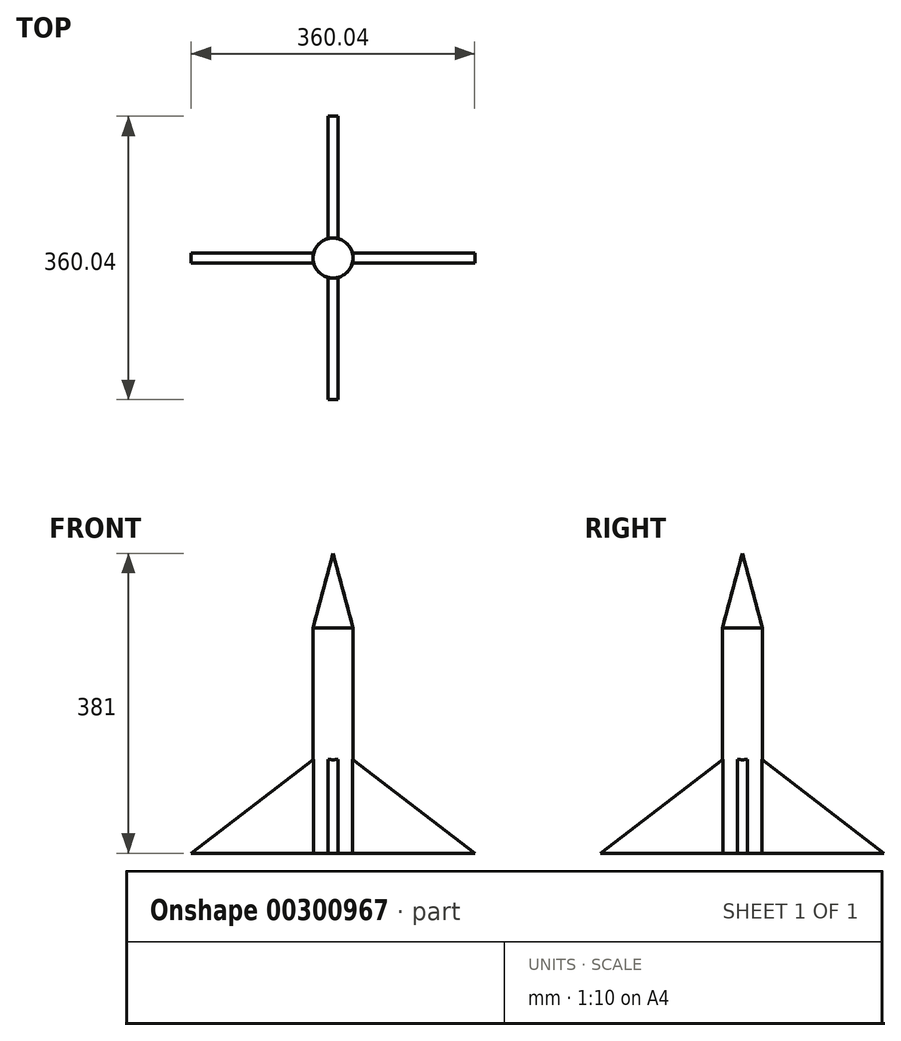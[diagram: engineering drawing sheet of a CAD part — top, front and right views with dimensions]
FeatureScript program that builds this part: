
annotation { "Feature Type Name" : "Feature", "Feature Type Description" : "" }
export const myFeature = defineFeature(function(context is Context, id is Id, definition is map)
    precondition{}
    {
        {
            var Q0;
            Q0=qCreatedBy(makeId("Top.planeOp"),FACE);
            var sketch = newSketch(context, id + "F0", { "sketchPlane" : qUnion([Q0])});
            skCircle(sketch, "E0", {"center": v(0, 0) * mm, "radius": 25.4 * mm});
            skSolve(sketch);
        }
        {
            var Q0;
            Q0 = qSketchRegion(id + "F0", true);
            extrude(context, id + "F1", {"entities" : qUnion([Q0]), "depth" : 381 * mm});
        }
        {
            var Q0;
            Q0=makeQuery(id+"F1.opExtrude","CAP_EDGE",EDGE,{"disambiguationData":[OSD([sQuery(id+"F0.wireOp",EDGE,"E0")])],"isStart":false});
            chamfer(context, id + "F2", {"entities" : qUnion([Q0]), "chamferType" : ChamferType.OFFSET_ANGLE, "width" : 25.4 * mm, "oppositeDirection" : false, "angle" : 75 * degree, "tangentPropagation" : true});
        }
        {
            var Q0;
            Q0=qCreatedBy(makeId("Front.planeOp"),FACE);
            var sketch = newSketch(context, id + "F3", { "sketchPlane" : qUnion([Q0])});
            skLineSegment(sketch, "E1", {"start": v(0, 138.23) * mm, "end": v(0, 0) * mm});
            skLineSegment(sketch, "E2", {"start": v(180.02, 0) * mm, "end": v(0, 0) * mm});
            skLineSegment(sketch, "E3", {"start": v(-129.4, 68.74) * mm, "end": v(-118.85, 63.14) * mm});
            skLineSegment(sketch, "E4", {"start": v(0, 138.23) * mm, "end": v(180.02, 0) * mm});
            skSolve(sketch);
        }
        {
            var Q0;
            Q0 = qSketchRegion(id + "F3", true);
            extrude(context, id + "F4", {"entities" : qUnion([Q0]), "operationType" : NewBodyOperationType.ADD, "endBound" : BoundingType.SYMMETRIC, "depth" : 12.7 * mm});
        }
        {
            var Q0;
            Q0=makeQuery(id+"F1.opExtrude","SWEPT_BODY",BODY,{"disambiguationData":[OSD([sQuery(id+"F0.wireOp",EDGE,"E0")])]});
            var Q1;
            Q1=makeQuery(id+"F1.opExtrude","SWEPT_FACE",FACE,{"disambiguationData":[OSD([sQuery(id+"F0.wireOp",EDGE,"E0")])]});
            circularPattern(context, id + "F5", {"entities" : qUnion([Q0]), "axis" : qUnion([Q1]), "angle" : 360 * degree, "instanceCount" : 4, "equalSpace" : true});
        }
    });
